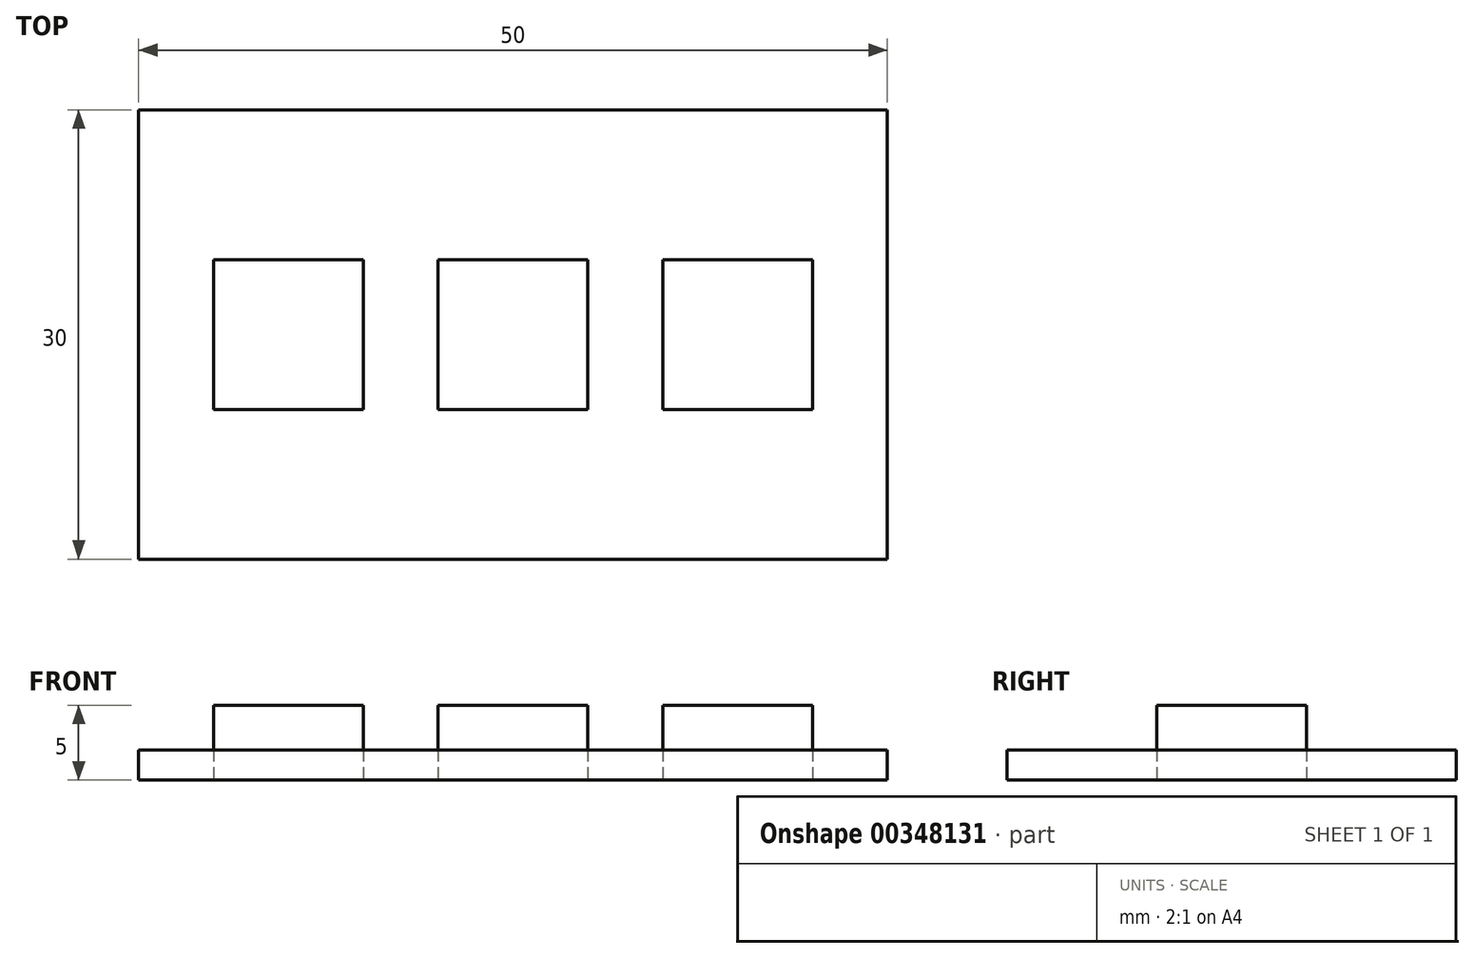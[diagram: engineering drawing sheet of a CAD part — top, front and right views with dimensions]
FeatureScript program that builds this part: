
annotation { "Feature Type Name" : "Feature", "Feature Type Description" : "" }
export const myFeature = defineFeature(function(context is Context, id is Id, definition is map)
    precondition{}
    {
        {
            var Q0;
            Q0=qCreatedBy(makeId("Top.planeOp"),FACE);
            var sketch = newSketch(context, id + "F0", { "sketchPlane" : qUnion([Q0])});
            skLineSegment(sketch, "E0.bottom", {"start": v(-25, 15) * mm, "end": v(25, 15) * mm});
            skLineSegment(sketch, "E0.top", {"start": v(-25, -15) * mm, "end": v(25, -15) * mm});
            skLineSegment(sketch, "E0.left", {"start": v(-25, 15) * mm, "end": v(-25, -15) * mm});
            skLineSegment(sketch, "E0.right", {"start": v(25, 15) * mm, "end": v(25, -15) * mm});
            skLineSegment(sketch, "E1", {"start": v(0, -15) * mm, "end": v(0, 15) * mm, "construction": true});
            skLineSegment(sketch, "E2", {"start": v(-25, 0) * mm, "end": v(25, 0) * mm, "construction": true});
            skLineSegment(sketch, "E3.bottom", {"start": v(-20, 5) * mm, "end": v(-10, 5) * mm});
            skLineSegment(sketch, "E3.top", {"start": v(-20, -5) * mm, "end": v(-10, -5) * mm});
            skLineSegment(sketch, "E3.left", {"start": v(-20, 5) * mm, "end": v(-20, -5) * mm});
            skLineSegment(sketch, "E3.right", {"start": v(-10, 5) * mm, "end": v(-10, -5) * mm});
            skLineSegment(sketch, "E4", {"start": v(-20, 0) * mm, "end": v(-10, 0) * mm, "construction": true});
            skLineSegment(sketch, "E5", {"start": v(-15, 5) * mm, "end": v(-15, -5) * mm, "construction": true});
            skLineSegment(sketch, "E6", {"start": v(-15, 0) * mm, "end": v(-15, -15) * mm, "construction": true});
            skSolve(sketch);
        }
        {
            var Q0;
            Q0=makeQuery(id+"F0.imprint","IMPRINT",FACE,{"disambiguationData":[TD([[makeQuery(id+"F0.imprint","IMPRINT",EDGE,{"derivedFrom":sQuery(id+"F0.wireOp",EDGE,"E3.bottom")}),-1.0]])]});
            extrude(context, id + "F1", {"entities" : qUnion([Q0]), "depth" : 5 * mm});
        }
        {
            var Q0;
            Q0=makeQuery(id+"F0.imprint","IMPRINT",FACE,{"disambiguationData":[TD([[makeQuery(id+"F0.imprint","IMPRINT",EDGE,{"derivedFrom":sQuery(id+"F0.wireOp",EDGE,"E0.bottom")}),-1.0]])]});
            var Q1;
            Q1=makeQuery(id+"F0.imprint","IMPRINT",FACE,{"disambiguationData":[TD([[makeQuery(id+"F0.imprint","IMPRINT",EDGE,{"derivedFrom":sQuery(id+"F0.wireOp",EDGE,"E3.bottom")}),-1.0]])]});
            extrude(context, id + "F2", {"entities" : qUnion([Q0, Q1]), "depth" : 2 * mm});
        }
        {
            var Q0;
            Q0=makeQuery(id+"F1.opExtrude","SWEPT_BODY",BODY,{"disambiguationData":[OSD([sQuery(id+"F0.wireOp",EDGE,"E3.bottom"),sQuery(id+"F0.wireOp",EDGE,"E3.top"),sQuery(id+"F0.wireOp",EDGE,"E3.left"),sQuery(id+"F0.wireOp",EDGE,"E3.right")])]});
            var Q1;
            Q1=makeQuery(id+"F2.opExtrude","SWEPT_FACE",FACE,{"disambiguationData":[OSD([sQuery(id+"F0.wireOp",EDGE,"E0.right")])]});
            transform(context, id + "F3", {"entities" : qUnion([Q0]), "transformType" : TransformType.TRANSLATION_DISTANCE, "transformDirection" : qUnion([Q1]), "distance" : 15 * mm, "makeCopy" : true});
        }
        {
            var Q0;
            Q0=makeQuery(id+"F3.opPattern","COPY",BODY,{"derivedFrom":makeQuery(id+"F1.opExtrude","SWEPT_BODY",BODY,{"disambiguationData":[OSD([sQuery(id+"F0.wireOp",EDGE,"E3.bottom"),sQuery(id+"F0.wireOp",EDGE,"E3.top"),sQuery(id+"F0.wireOp",EDGE,"E3.left"),sQuery(id+"F0.wireOp",EDGE,"E3.right")])]}),"instanceName":"1"});
            var Q1;
            Q1=makeQuery(id+"F3.opPattern","COPY",FACE,{"derivedFrom":makeQuery(id+"F1.opExtrude","SWEPT_FACE",FACE,{"disambiguationData":[OSD([sQuery(id+"F0.wireOp",EDGE,"E3.right")])]}),"instanceName":"1"});
            transform(context, id + "F4", {"entities" : qUnion([Q0]), "transformType" : TransformType.TRANSLATION_DISTANCE, "transformDirection" : qUnion([Q1]), "distance" : 15 * mm, "makeCopy" : true});
        }
    });
